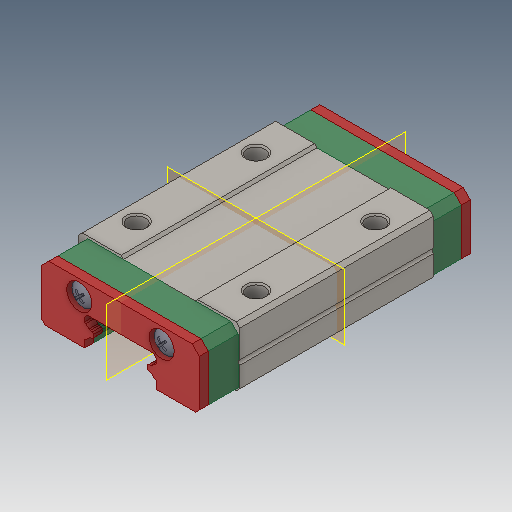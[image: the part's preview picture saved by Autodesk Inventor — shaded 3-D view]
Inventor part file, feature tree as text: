
AUTODESK INVENTOR PART (.ipt)
format: ipt  version: 2019.4 (Build 234330000, 330)  size: 473,088 bytes
history: imported  units: mm
features: other x9, plane x2, imported_body x1
ambient origin geometry x8: Origin, YZ Plane, XZ Plane, XY Plane, X Axis, Y Axis, Z Axis, Center Point
bodies: Solid1 (imported_parasolid), Solid2 (imported_parasolid), Solid3 (imported_parasolid), Solid4 (imported_parasolid), Solid5 (imported_parasolid), Solid6 (imported_parasolid), Solid7 (imported_parasolid), Solid8 (imported_parasolid), Solid9 (imported_parasolid)
feature tree (12):
  plane  "Work Plane1"
  plane  "Work Plane2"
  other  "MID BODY, MGN 12H, LINEAR GUIDE BLOCK-1-solid1"
  other  "MID BODY, MGN 12H, LINEAR GUIDE BLOCK-1-solid2"
  other  "MID BODY, MGN 12H, LINEAR GUIDE BLOCK-1-solid3"
  other  "MID BODY, MGN 12H, LINEAR GUIDE BLOCK-1-solid4"
  other  "MID BODY, MGN 12H, LINEAR GUIDE BLOCK-1-solid5"
  other  "SCREW HEAD, MGN 12H, LINEAR GUIDE BLOCK-1-solid1"
  other  "SCREW HEAD, MGN 12H, LINEAR GUIDE BLOCK-2-solid1"
  other  "SCREW HEAD, MGN 12H, LINEAR GUIDE BLOCK-3-solid1"
  other  "SCREW HEAD, MGN 12H, LINEAR GUIDE BLOCK-4-solid1"
  imported_body  NMx_Import_Brep_tag  [imported B-rep: ~50 faces, bbox_mm=[19.044812, 8.226555, 32.4]]
